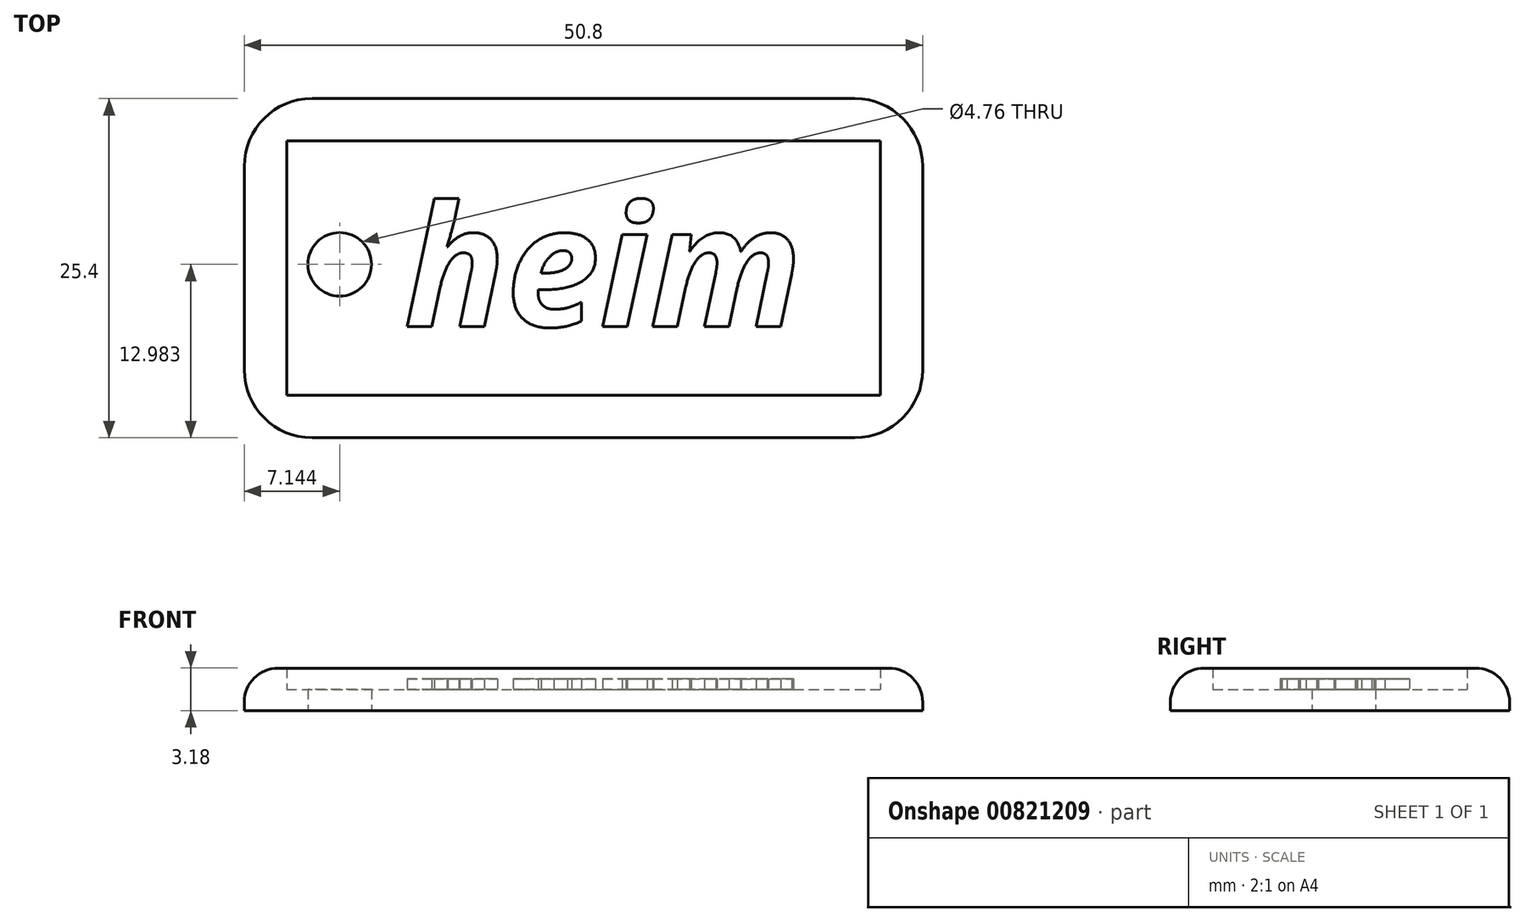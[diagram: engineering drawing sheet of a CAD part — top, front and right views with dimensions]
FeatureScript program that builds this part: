
annotation { "Feature Type Name" : "Feature", "Feature Type Description" : "" }
export const myFeature = defineFeature(function(context is Context, id is Id, definition is map)
    precondition{}
    {
        {
            var Q0;
            Q0=qCreatedBy(makeId("Top.planeOp"),FACE);
            var sketch = newSketch(context, id + "F0", { "sketchPlane" : qUnion([Q0])});
            skLineSegment(sketch, "E0.bottom", {"start": v(0, 0) * mm, "end": v(50.8, 0) * mm});
            skLineSegment(sketch, "E0.top", {"start": v(0, 25.4) * mm, "end": v(50.8, 25.4) * mm});
            skLineSegment(sketch, "E0.left", {"start": v(0, 0) * mm, "end": v(0, 25.4) * mm});
            skLineSegment(sketch, "E0.right", {"start": v(50.8, 0) * mm, "end": v(50.8, 25.4) * mm});
            skCircle(sketch, "E1", {"center": v(7.14, 12.98) * mm, "radius": 2.38 * mm});
            skLineSegment(sketch, "E2.0", {"start": v(3.17, 22.23) * mm, "end": v(47.62, 22.23) * mm});
            skLineSegment(sketch, "E2.1", {"start": v(3.17, 3.18) * mm, "end": v(3.17, 22.23) * mm});
            skLineSegment(sketch, "E2.2", {"start": v(3.18, 3.18) * mm, "end": v(47.62, 3.18) * mm});
            skLineSegment(sketch, "E2.3", {"start": v(47.62, 3.18) * mm, "end": v(47.62, 22.23) * mm});
            skSolve(sketch);
        }
        {
            var Q0;
            Q0=makeQuery(id+"F0.imprint","IMPRINT",FACE,{"disambiguationData":[TD([[makeQuery(id+"F0.imprint","IMPRINT",EDGE,{"derivedFrom":sQuery(id+"F0.wireOp",EDGE,"E1")}),-1.0]])]});
            extrude(context, id + "F1", {"entities" : qUnion([Q0]), "depth" : 1.59 * mm, "offsetDistance" : 25.4 * mm});
        }
        {
            var Q0;
            Q0 = qSketchRegion(id + "F0", true);
            extrude(context, id + "F2", {"entities" : qUnion([Q0]), "operationType" : NewBodyOperationType.ADD, "depth" : 3.17 * mm, "offsetDistance" : 25.4 * mm});
        }
        {
            var Q0;
            Q0=makeQuery(id+"F2.opExtrude","SWEPT_EDGE",EDGE,{"disambiguationData":[OSD([sQuery(id+"F0.wireOp",EDGE,"E0.bottom"),sQuery(id+"F0.wireOp",EDGE,"E0.right")])]});
            var Q1;
            Q1=makeQuery(id+"F2.opExtrude","SWEPT_EDGE",EDGE,{"disambiguationData":[OSD([sQuery(id+"F0.wireOp",EDGE,"E0.top"),sQuery(id+"F0.wireOp",EDGE,"E0.right")])]});
            var Q2;
            Q2=makeQuery(id+"F2.opExtrude","SWEPT_EDGE",EDGE,{"disambiguationData":[OSD([sQuery(id+"F0.wireOp",EDGE,"E0.top"),sQuery(id+"F0.wireOp",EDGE,"E0.left")])]});
            var Q3;
            Q3=makeQuery(id+"F2.opExtrude","SWEPT_EDGE",EDGE,{"disambiguationData":[OSD([sQuery(id+"F0.wireOp",EDGE,"E0.bottom"),sQuery(id+"F0.wireOp",EDGE,"E0.left")])]});
            fillet(context, id + "F3", {"entities" : qUnion([Q0, Q1, Q2, Q3]), "radius" : 5.08 * mm, "tangentPropagation" : true, "allowEdgeOverflow" : false});
        }
        {
            var Q0;
            Q0=makeQuery(id+"F2.opExtrude","CAP_EDGE",EDGE,{"disambiguationData":[OSD([sQuery(id+"F0.wireOp",EDGE,"E0.top")])],"isStart":false});
            fillet(context, id + "F4", {"entities" : qUnion([Q0]), "radius" : 2.54 * mm, "tangentPropagation" : true, "allowEdgeOverflow" : false});
        }
        {
            var Q0;
            Q0=makeQuery(id+"F1.opExtrude","CAP_FACE",FACE,{"disambiguationData":[OSD([sQuery(id+"F0.wireOp",EDGE,"E1"),sQuery(id+"F0.wireOp",EDGE,"E2.0"),sQuery(id+"F0.wireOp",EDGE,"E2.1"),sQuery(id+"F0.wireOp",EDGE,"E2.2"),sQuery(id+"F0.wireOp",EDGE,"E2.3")])],"isStart":false});
            var sketch = newSketch(context, id + "F5", { "sketchPlane" : qUnion([Q0])});
            skText(sketch, "E3", { "text": "heim", "fontName": "OpenSans-BoldItalic.ttf"});
            const initialGuessF5  = {"E3": [0.01197, 0.00834, 1, 0, 0.00908]};
            skSetInitialGuess(sketch, initialGuessF5);
            skSolve(sketch);
        }
        {
            var Q0;
            Q0 = qSketchRegion(id + "F5", true);
            extrude(context, id + "F6", {"entities" : qUnion([Q0]), "operationType" : NewBodyOperationType.ADD, "depth" : 0.8 * mm, "offsetDistance" : 25.4 * mm});
        }
    });
